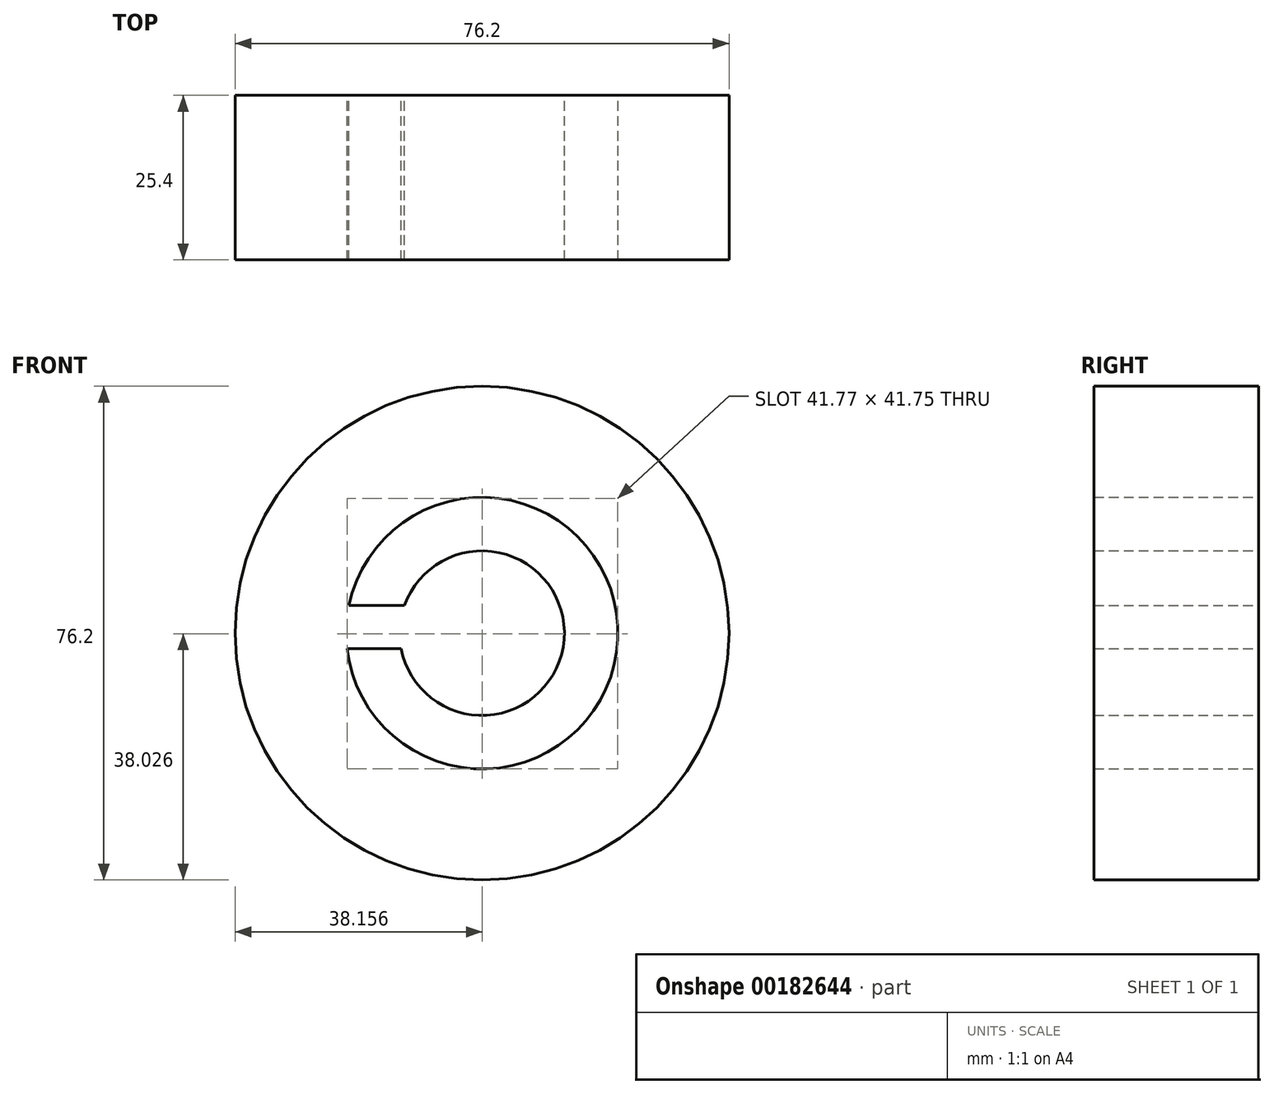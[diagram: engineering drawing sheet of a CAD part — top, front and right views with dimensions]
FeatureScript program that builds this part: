
annotation { "Feature Type Name" : "Feature", "Feature Type Description" : "" }
export const myFeature = defineFeature(function(context is Context, id is Id, definition is map)
    precondition{}
    {
        {
            var Q0;
            Q0=qCreatedBy(makeId("Front.planeOp"),FACE);
            var sketch = newSketch(context, id + "F0", { "sketchPlane" : qUnion([Q0])});
            skCircle(sketch, "E0", {"center": v(-16.7, 2.37) * mm, "radius": 38.1 * mm});
            skCircle(sketch, "E1", {"center": v(-16.7, 2.37) * mm, "radius": 20.96 * mm});
            skCircle(sketch, "E2", {"center": v(-16.7, 2.37) * mm, "radius": 12.7 * mm});
            skPoint(sketch, "E3.middle", {"position": v(-28.96, 11.84) * mm});
            skLineSegment(sketch, "E4", {"start": v(-37.22, 6.62) * mm, "end": v(-28.66, 6.62) * mm});
            skLineSegment(sketch, "E5", {"start": v(-37.52, 0) * mm, "end": v(-29.17, 0) * mm});
            skSolve(sketch);
        }
        {
            var Q0;
            Q0 = qSketchRegion(id + "F0", true);
            var Q1;
            {var subQ0=sQuery(id+"F0.wireOp",EDGE,"E2");var subQ1=makeQuery(id+"F0.imprint","INTERSECT",VERTEX,{"derivedFrom":[subQ0,sQuery(id+"F0.wireOp",EDGE,"E4")]});Q1=makeQuery(id+"F0.imprint","IMPRINT",FACE,{"disambiguationData":[TD([[makeQuery(id+"F0.imprint","IMPRINT",EDGE,{"disambiguationData":[TD([[subQ1,-1.0]])],"derivedFrom":subQ0}),1.0]])]});}
            var Q2;
            {var subQ0=sQuery(id+"F0.wireOp",EDGE,"E4");Q2=makeQuery(id+"F0.imprint","IMPRINT",FACE,{"disambiguationData":[TD([[makeQuery(id+"F0.imprint","IMPRINT",EDGE,{"derivedFrom":subQ0}),-1.0]])]});}
            extrude(context, id + "F1", {"entities" : qUnion([Q0, Q1, Q2]), "depth" : 25.4 * mm});
        }
    });
